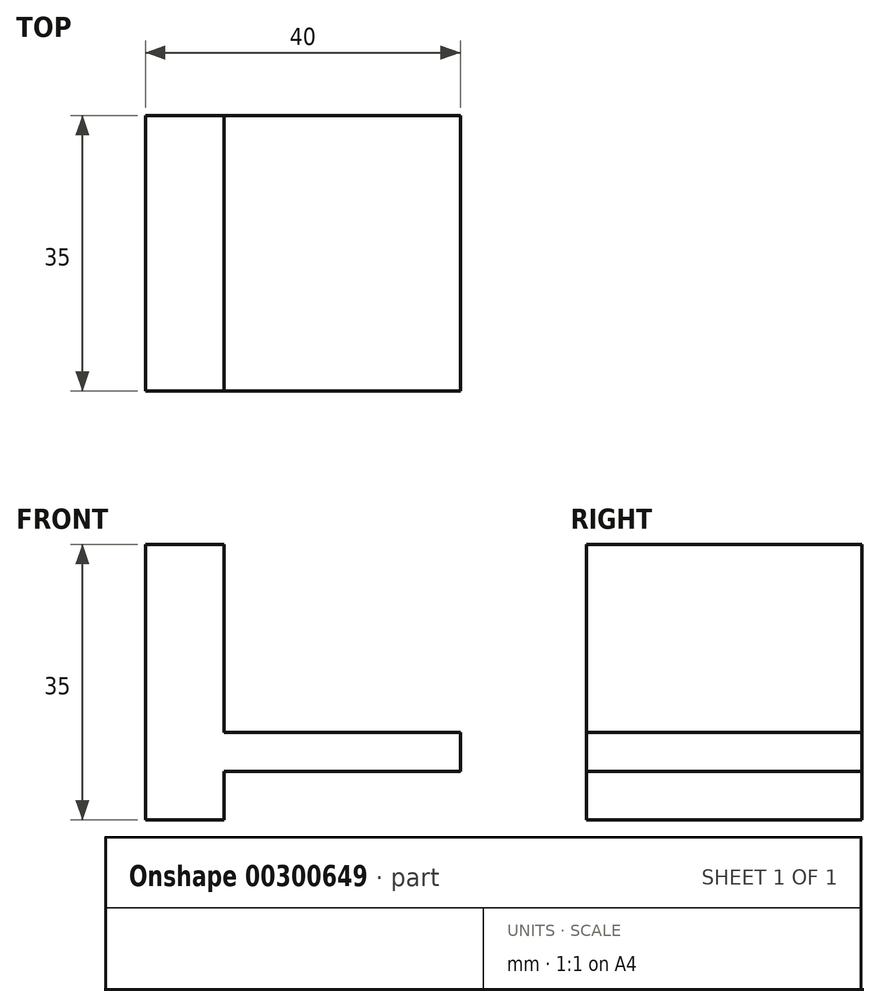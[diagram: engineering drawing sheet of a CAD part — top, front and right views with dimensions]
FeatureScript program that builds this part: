
annotation { "Feature Type Name" : "Feature", "Feature Type Description" : "" }
export const myFeature = defineFeature(function(context is Context, id is Id, definition is map)
    precondition{}
    {
        {
            var Q0;
            Q0=qCreatedBy(makeId("Front.planeOp"),FACE);
            var sketch = newSketch(context, id + "F0", { "sketchPlane" : qUnion([Q0])});
            skLineSegment(sketch, "E0.top", {"start": v(32.5, -20) * mm, "end": v(-32.5, -20) * mm});
            skLineSegment(sketch, "E0.right", {"start": v(-32.5, 20) * mm, "end": v(-32.5, -20) * mm});
            skPoint(sketch, "E0.middle", {"position": v(0, 0) * mm});
            skLineSegment(sketch, "E1", {"start": v(-7.5, 20) * mm, "end": v(32.5, 0) * mm});
            skLineSegment(sketch, "E2.bottom", {"start": v(-32.5, -20) * mm, "end": v(-22.5, -20) * mm});
            skLineSegment(sketch, "E2.top", {"start": v(-32.5, 15) * mm, "end": v(-22.5, 15) * mm});
            skLineSegment(sketch, "E2.left", {"start": v(-32.5, -20) * mm, "end": v(-32.5, 15) * mm});
            skLineSegment(sketch, "E2.right", {"start": v(-22.5, -20) * mm, "end": v(-22.5, 15) * mm});
            skLineSegment(sketch, "E3.bottom", {"start": v(-22.5, -8.85) * mm, "end": v(7.5, -8.85) * mm});
            skLineSegment(sketch, "E3.top", {"start": v(-22.5, -13.85) * mm, "end": v(7.5, -13.85) * mm});
            skLineSegment(sketch, "E3.left", {"start": v(-22.5, -8.85) * mm, "end": v(-22.5, -13.85) * mm});
            skLineSegment(sketch, "E3.right", {"start": v(7.5, -8.85) * mm, "end": v(7.5, -13.85) * mm});
            skLineSegment(sketch, "E4", {"start": v(-32.5, 20) * mm, "end": v(-7.5, 20) * mm});
            skLineSegment(sketch, "E5", {"start": v(32.5, 0) * mm, "end": v(32.5, -20) * mm});
            skLineSegment(sketch, "E6.bottom", {"start": v(-32.5, 0) * mm, "end": v(-22.5, 0) * mm});
            skLineSegment(sketch, "E6.left", {"start": v(-32.5, 0) * mm, "end": v(-32.5, -20) * mm});
            skLineSegment(sketch, "E6.right", {"start": v(-22.5, 0) * mm, "end": v(-22.5, -20) * mm});
            skSolve(sketch);
        }
        {
            var Q0;
            {var subQ3=sQuery(id+"F0.wireOp",EDGE,"E0.top");Q0=makeQuery(id+"F0.imprint","IMPRINT",FACE,{"disambiguationData":[TD([[makeQuery(id+"F0.imprint","IMPRINT",EDGE,{"derivedFrom":subQ3}),-1.0]])]});}
            extrude(context, id + "F1", {"entities" : qUnion([Q0]), "depth" : 10 * mm});
        }
        {
            var Q0;
            {var subQ1=sQuery(id+"F0.wireOp",EDGE,"E6.bottom");Q0=makeQuery(id+"F0.imprint","IMPRINT",FACE,{"disambiguationData":[TD([[makeQuery(id+"F0.imprint","IMPRINT",EDGE,{"derivedFrom":subQ1}),-1.0]])]});}
            extrude(context, id + "F2", {"entities" : qUnion([Q0]), "operationType" : NewBodyOperationType.ADD, "depth" : 35 * mm});
        }
        {
            var Q0;
            Q0=makeQuery(id+"F0.imprint","IMPRINT",FACE,{"disambiguationData":[TD([[makeQuery(id+"F0.imprint","IMPRINT",EDGE,{"derivedFrom":sQuery(id+"F0.wireOp",EDGE,"E2.top")}),-1.0]])]});
            extrude(context, id + "F3", {"entities" : qUnion([Q0]), "operationType" : NewBodyOperationType.ADD, "depth" : 35 * mm});
        }
        {
            var Q0;
            {var subQ0=sQuery(id+"F0.wireOp",EDGE,"E3.bottom");Q0=makeQuery(id+"F0.imprint","IMPRINT",FACE,{"disambiguationData":[TD([[makeQuery(id+"F0.imprint","IMPRINT",EDGE,{"derivedFrom":subQ0}),-1.0]])]});}
            extrude(context, id + "F4", {"entities" : qUnion([Q0]), "operationType" : NewBodyOperationType.ADD, "depth" : 35 * mm});
        }
    });
